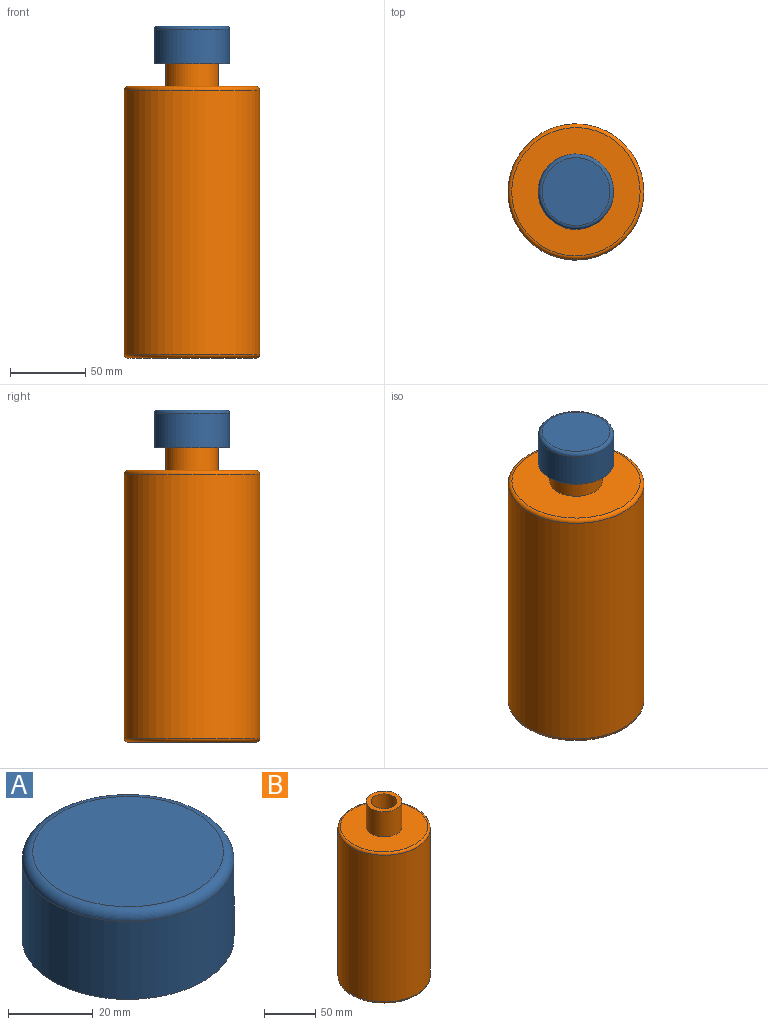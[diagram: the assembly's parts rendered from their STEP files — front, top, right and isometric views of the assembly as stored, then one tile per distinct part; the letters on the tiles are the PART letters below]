
ASSEMBLY  parts=2 mates=1
PART A: 6 faces, bbox 54.1x54.1x25 mm
  f0: cylinder r=25mm len=50mm, axis (0,0,-1), area 3534.3mm2, adj f2,f5
  f1: plane 45x45mm, normal (0,0,1), area 1590.4mm2, adj f5
  f2: plane 50x50mm, normal (0,0,-1), area 706.9mm2, adj f0,f3
  f3: cylinder r=20mm len=40mm, axis (0,0,-1), area 2513.3mm2, adj f2,f4
  f4: plane 40x40mm, normal (0,0,-1), area 1256.6mm2, adj f3
  f5: torus R=22.5mm, axis (0,0,1), area 594.4mm2, adj f0,f1
PART B: 11 faces, bbox 97.4x97.4x210 mm
  f0: cylinder r=45mm len=175mm, axis (0,0,-1), area 49480.1mm2, adj f9,f10
  f1: plane 85x85mm, normal (0,0,1), area 4712.4mm2, adj f3,f10
  f2: plane 85x85mm, normal (0,0,-1), area 5674.5mm2, adj f9
  f3: cylinder r=17.5mm len=35mm, axis (0,0,-1), area 3298.7mm2, adj f1,f4
  f4: plane 35x35mm, normal (0,0,1), area 471.2mm2, adj f3,f8
  f5: cylinder r=40mm len=170mm, axis (0,0,-1), area 42725.7mm2, adj f6,f7
  f6: plane 80x80mm, normal (0,0,-1), area 4535.7mm2, adj f5,f8
  f7: plane 80x80mm, normal (0,0,1), area 5026.5mm2, adj f5
  f8: cylinder r=12.5mm len=35mm, axis (0,0,-1), area 2748.9mm2, adj f4,f6
  f9: torus R=42.5mm, axis (0,0,1), area 1087.9mm2, adj f0,f2
  f10: torus R=42.5mm, axis (0,0,1), area 1087.9mm2, adj f0,f1
PLACE A t=(-13.23,19.44,130.62)mm
PLACE B t=(-13.23,19.44,-64.38)mm
MATE cylindrical A.f0 <-> B.f0  axis (0,0,-1) through (-13.23,19.44,130.62)mm
